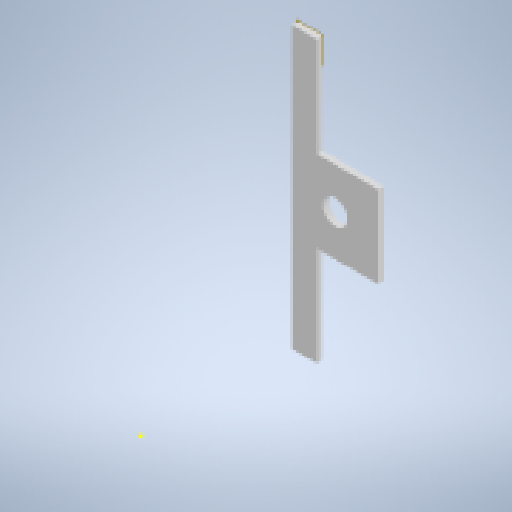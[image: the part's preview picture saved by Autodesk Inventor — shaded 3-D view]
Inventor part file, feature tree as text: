
AUTODESK INVENTOR PART (.ipt)
format: ipt  version: 2023.1 (Build 271208000, 208)  size: 164,864 bytes
history: native  units: mm
features: sketch x5, other x4, extrude x3, reference x2, projected_geometry x2, plane x1
ambient origin geometry x8: Origin, YZ Plane, XZ Plane, XY Plane, X Axis, Y Axis, Z Axis, Center Point
bodies: Solid1 (feature_tree)
feature tree (17):
  sketch  "Sketch1"  dims[d0=3.0mm d1=0.0mm d9=3.0mm]
  plane  "Work Plane1"
  extrude  "Extrusion1"  Depth=3.0mm
  extrude  "Extrusion4"  Depth=30.0mm TaperAngle=0.0deg
  sketch  "Sketch6"  dims[d15=30.0mm d16=0.0mm]
  extrude  "Extrusion5"  Depth=12.0mm
  sketch  "Sketch2"  dims[d10=40.0mm d11=30.0mm d12=0.0mm]
  reference  "Reference1"
  reference  "Reference2"
  sketch  "Sketch5"  dims[d13=12.0mm d14=9.0mm]
  projected_geometry  "Projected Loop3"
  sketch  "Sketch7"
  projected_geometry  "Projected Loop4"
  parser-record x1  (decoder bookkeeping rows leaked as tree rows — omitted from the tree; the rows remain in map.json)
  other  "Main Assembly.iam"
  other  "12 mm rod:1"
  other  "12 mm rod:2"
note: 1 file-system path scrubbed to <path> (originals preserved in map.json)
